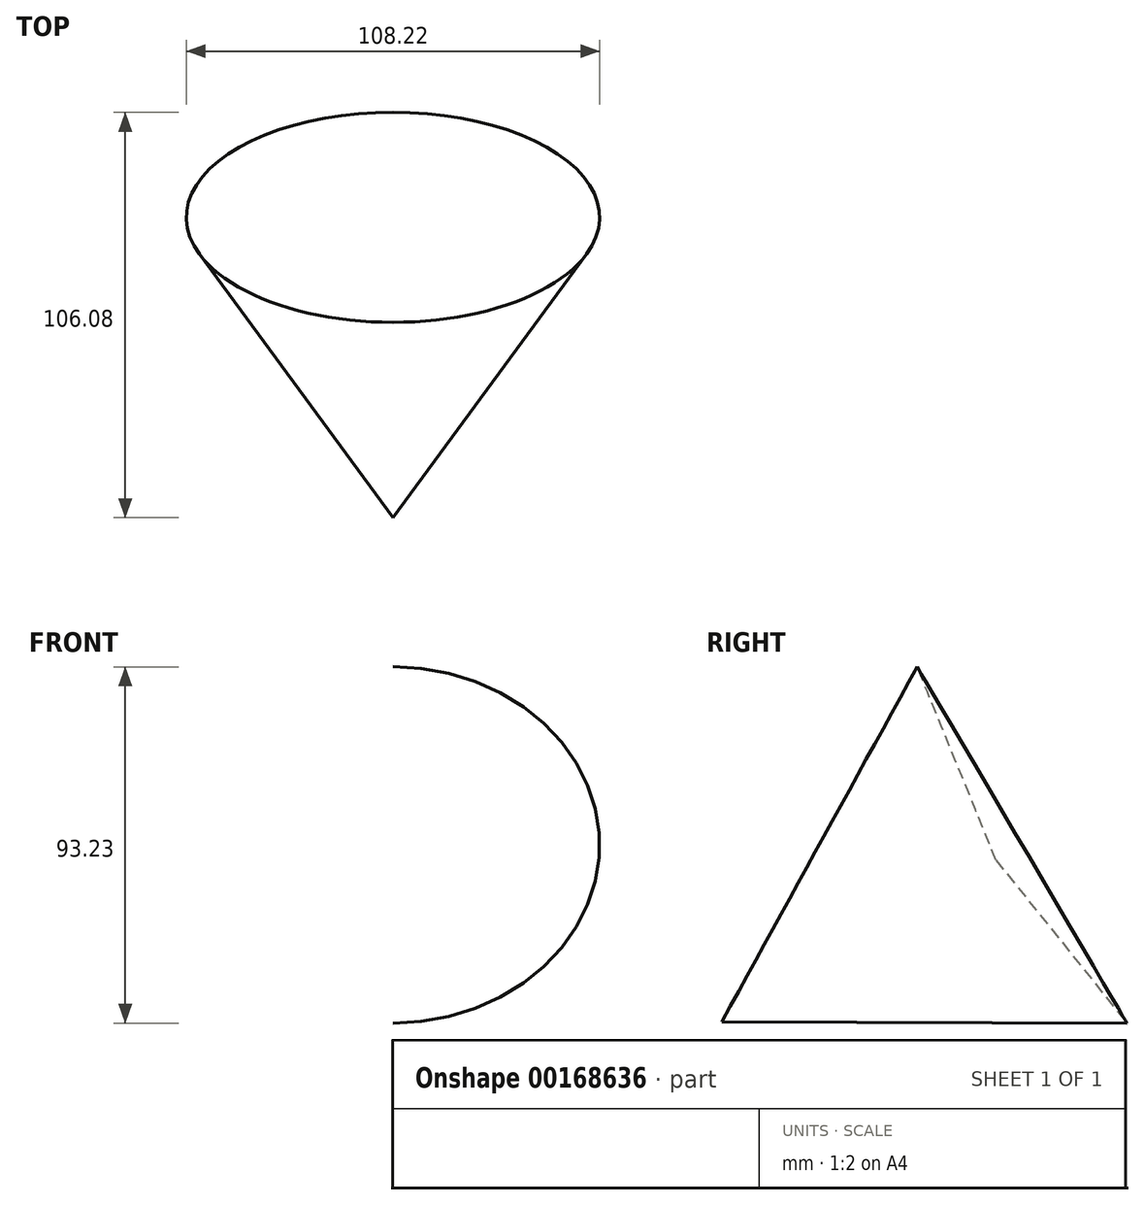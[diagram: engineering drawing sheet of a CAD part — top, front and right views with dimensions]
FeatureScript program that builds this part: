
annotation { "Feature Type Name" : "Feature", "Feature Type Description" : "" }
export const myFeature = defineFeature(function(context is Context, id is Id, definition is map)
    precondition{}
    {
        {
            var Q0;
            Q0=qCreatedBy(makeId("Right.planeOp"),FACE);
            var sketch = newSketch(context, id + "F0", { "sketchPlane" : qUnion([Q0])});
            skLineSegment(sketch, "E0", {"start": v(33.82, 56.47) * mm, "end": v(68.1, 13.86) * mm});
            skLineSegment(sketch, "E1", {"start": v(68.1, 13.86) * mm, "end": v(-38, 14.15) * mm});
            skLineSegment(sketch, "E2", {"start": v(-38, 14.15) * mm, "end": v(33.82, 56.47) * mm});
            skSolve(sketch);
        }
        {
            var Q0;
            Q0=makeQuery(id+"F0.imprint","IMPRINT",FACE,{"disambiguationData":[TD([[makeQuery(id+"F0.imprint","IMPRINT",EDGE,{"derivedFrom":sQuery(id+"F0.wireOp",EDGE,"E0")}),-1.0]])]});
            var Q1;
            Q1=sQuery(id+"F0.wireOp",EDGE,"E2");
            revolve(context, id + "F1", {"entities" : qUnion([Q0]), "axis" : qUnion([Q1]), "revolveType" : RevolveType.FULL});
        }
    });
